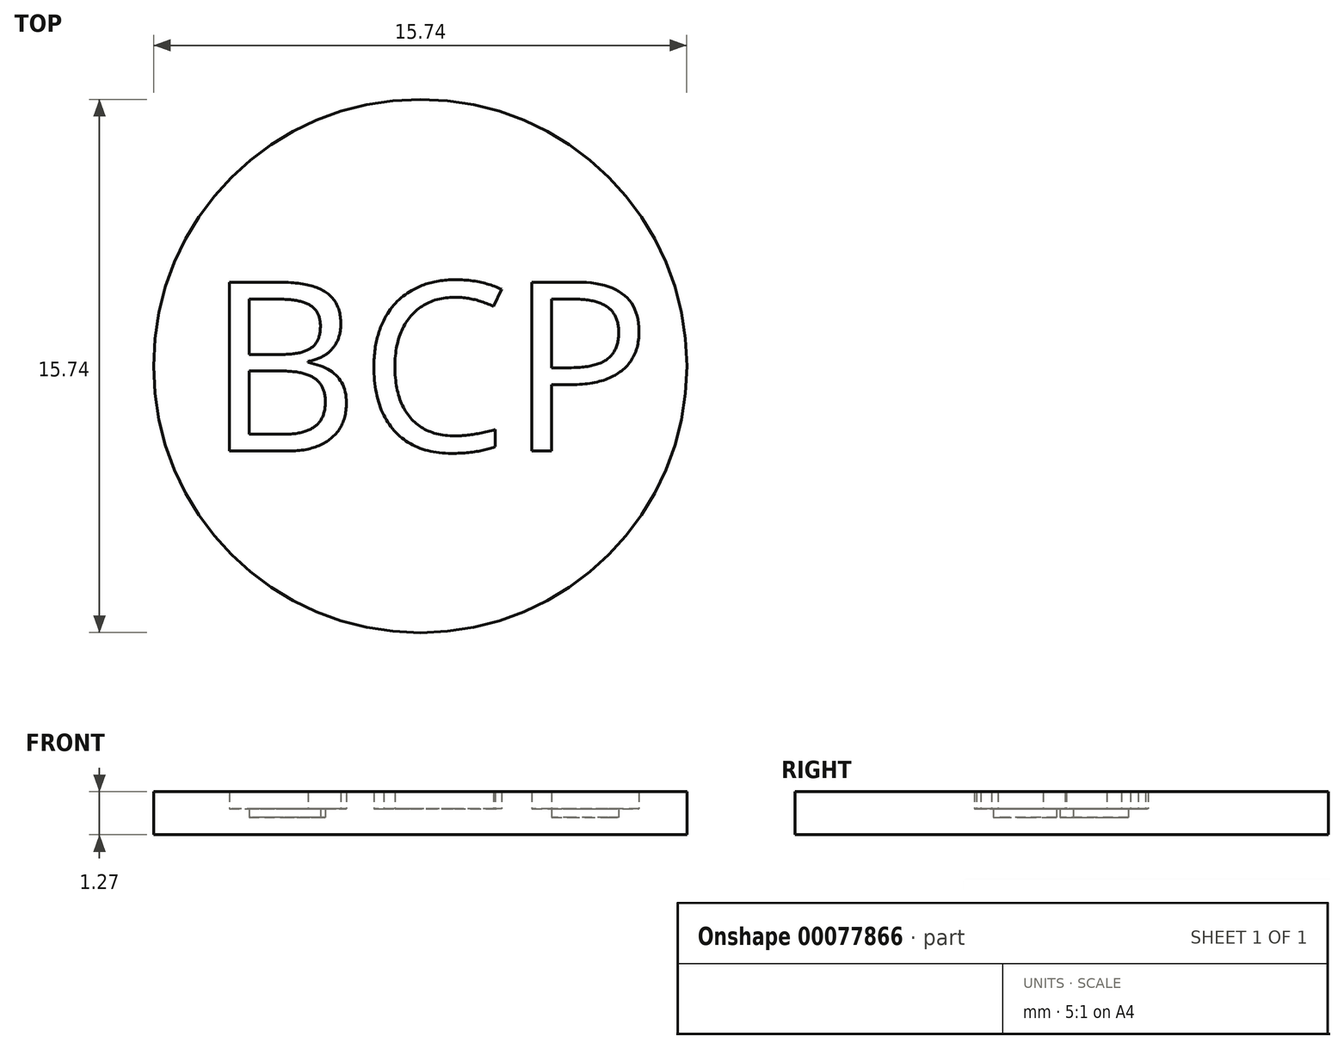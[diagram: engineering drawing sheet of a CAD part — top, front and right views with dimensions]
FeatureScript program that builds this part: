
annotation { "Feature Type Name" : "Feature", "Feature Type Description" : "" }
export const myFeature = defineFeature(function(context is Context, id is Id, definition is map)
    precondition{}
    {
        {
            var Q0;
            Q0=qCreatedBy(makeId("Top.planeOp"),FACE);
            var sketch = newSketch(context, id + "F0", { "sketchPlane" : qUnion([Q0])});
            skCircle(sketch, "E0", {"center": v(0, 0) * mm, "radius": 7.87 * mm});
            skText(sketch, "E1", { "text": "BCP", "fontName": "OpenSans-Regular.ttf"});
            const initialGuessF0  = {"E1": [-0.00632, -0.00251, 1, 0, 0.00503]};
            skSetInitialGuess(sketch, initialGuessF0);
            skSolve(sketch);
        }
        {
            var Q0;
            Q0=makeQuery(id+"F0.imprint","IMPRINT",FACE,{"disambiguationData":[TD([[makeQuery(id+"F0.imprint","IMPRINT",EDGE,{"derivedFrom":sQuery(id+"F0.wireOp",EDGE,"E0")}),1.0]])]});
            extrude(context, id + "F1", {"entities" : qUnion([Q0]), "depth" : 1.27 * mm});
        }
        {
            var Q0;
            Q0=makeQuery(id+"F0.imprint","IMPRINT",FACE,{"disambiguationData":[TD([[makeQuery(id+"F0.imprint","IMPRINT",EDGE,{"derivedFrom":sQuery(id+"F0.wireOp",EDGE,"E1.sketch_text.stroke-25")}),-1.0]])]});
            var Q1;
            Q1=makeQuery(id+"F0.imprint","IMPRINT",FACE,{"disambiguationData":[TD([[makeQuery(id+"F0.imprint","IMPRINT",EDGE,{"derivedFrom":sQuery(id+"F0.wireOp",EDGE,"E1.sketch_text.stroke-40")}),-1.0]])]});
            var Q2;
            Q2=makeQuery(id+"F0.imprint","IMPRINT",FACE,{"disambiguationData":[TD([[makeQuery(id+"F0.imprint","IMPRINT",EDGE,{"derivedFrom":sQuery(id+"F0.wireOp",EDGE,"E1.sketch_text.stroke-0")}),-1.0]])]});
            extrude(context, id + "F2", {"entities" : qUnion([Q0, Q1, Q2]), "operationType" : NewBodyOperationType.ADD, "depth" : 0.76 * mm});
        }
        {
            var Q0;
            Q0=makeQuery(id+"F0.imprint","IMPRINT",FACE,{"disambiguationData":[TD([[makeQuery(id+"F0.imprint","IMPRINT",EDGE,{"derivedFrom":sQuery(id+"F0.wireOp",EDGE,"E1.sketch_text.stroke-18")}),1.0]])]});
            var Q1;
            Q1=makeQuery(id+"F0.imprint","IMPRINT",FACE,{"disambiguationData":[TD([[makeQuery(id+"F0.imprint","IMPRINT",EDGE,{"derivedFrom":sQuery(id+"F0.wireOp",EDGE,"E1.sketch_text.stroke-11")}),1.0]])]});
            var Q2;
            Q2=makeQuery(id+"F0.imprint","IMPRINT",FACE,{"disambiguationData":[TD([[makeQuery(id+"F0.imprint","IMPRINT",EDGE,{"derivedFrom":sQuery(id+"F0.wireOp",EDGE,"E1.sketch_text.stroke-48")}),1.0]])]});
            extrude(context, id + "F3", {"entities" : qUnion([Q0, Q1, Q2]), "operationType" : NewBodyOperationType.ADD, "depth" : 0.5 * mm});
        }
    });
